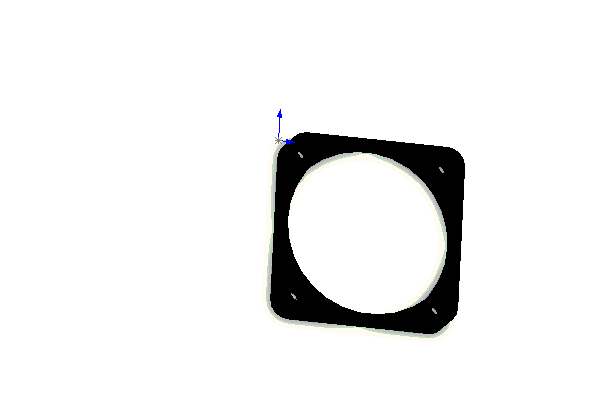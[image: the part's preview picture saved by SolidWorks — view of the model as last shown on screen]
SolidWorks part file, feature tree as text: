
SOLIDWORKS PART (.sldprt)
format: sldprt  version: not decoded by parser v0  size: 109,056 bytes
history: native  units: mm
features: sketch x3, cut_extrude x2, material x1, extrude x1 (+13 scaffold rows collapsed)
feature tree (20):
  scaffold x13  (default folders/planes/origin — collapsed)
  material  "Material <not specified>"
  sketch  "Sketch1"  dims[D3=4.0mm D4=4.0mm D1=40.0mm D2=40.0mm]
  extrude  "Extrude1"  Depth=10mm
  sketch  "Sketch2"  dims[D3=39.0mm D1=20.0mm D2=20.0mm]
  cut_extrude  "Cut-Extrude1"  Depth=20mm
  sketch  "Sketch4"  dims[D1=4.3mm D2=4.3mm D3=4.3mm D4=4.3mm D5=4.0mm D6=4.0mm D7=4.0mm D8=4.0mm]
  cut_extrude  "Cut-Extrude2"  Depth=20mm
decode coverage: 6 of 6 modeling features carry decoded parameters
note: suppression state not decoded; provenance and decode notes live in map.json
